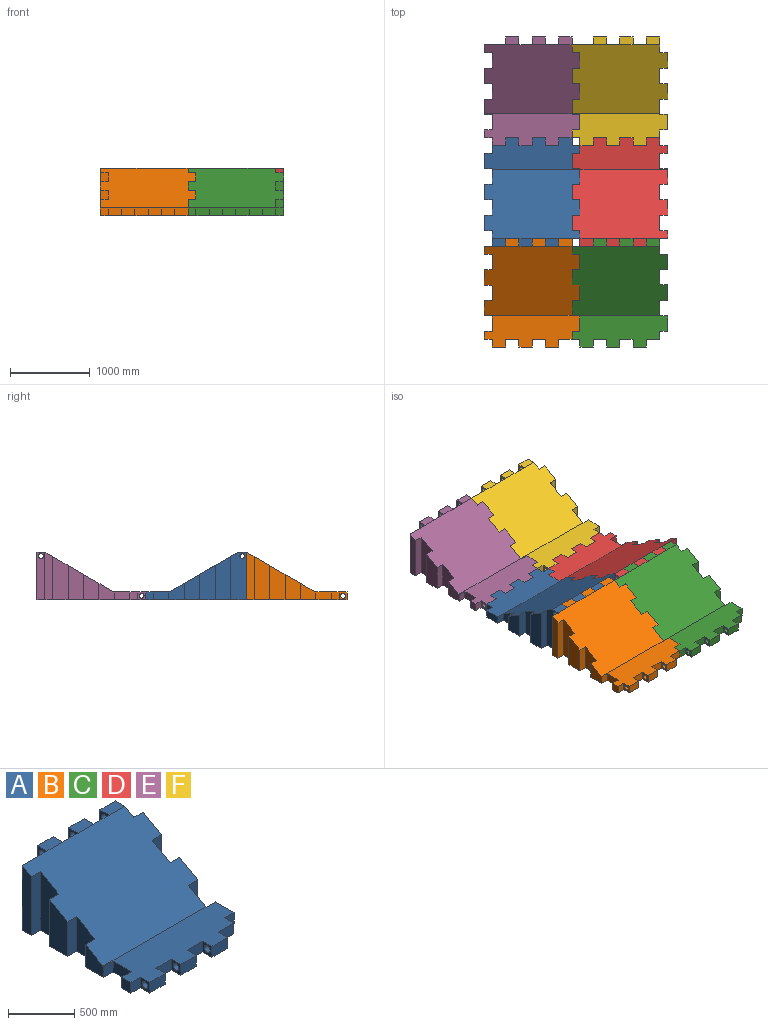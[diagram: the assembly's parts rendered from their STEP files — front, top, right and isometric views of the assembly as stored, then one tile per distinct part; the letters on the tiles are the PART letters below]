
ASSEMBLY  parts=6 mates=8
PART A: 62 faces, bbox 1200x1366x600 mm
  f0: cylinder r=30mm len=166.67mm, axis (-1,0,0), area 31415.9mm2, adj f1,f6
  f1: plane 100x100mm, normal (-1,0,0), area 7172.6mm2, adj f0,f3,f11,f14,f19
  f2: plane 100x100mm, normal (1,0,0), area 7172.6mm2, adj f3,f13,f14,f19,f54
  f3: plane 166.67x100mm, normal (0,-1,0), area 16666.7mm2, adj f1,f2,f14,f19
  f4: plane 100x100mm, normal (0,-1,0), area 10000mm2, adj f5,f14,f19,f20
  f5: plane 100x97.17mm, normal (1,0,0), area 9716.9mm2, adj f4,f7,f14,f19
  f6: plane 100x100mm, normal (1,0,0), area 7172.6mm2, adj f0,f7,f11,f14,f19
  f7: plane 166.67x100mm, normal (0,-1,0), area 16666.7mm2, adj f5,f6,f14,f19
  f8: plane 600x166.67mm, normal (0,1,0), area 100000mm2, adj f14,f15,f49,f52
  f9: plane 600x166.67mm, normal (0,1,0), area 100000mm2, adj f14,f16,f45,f48
  f10: plane 600x166.67mm, normal (0,1,0), area 100000mm2, adj f14,f17,f42,f44
  f11: plane 166.67x100mm, normal (0,-1,0), area 16666.7mm2, adj f1,f6,f14,f19
  f12: plane 166.67x100mm, normal (0,-1,0), area 16666.7mm2, adj f14,f19,f56,f59
  f13: plane 166.67x100mm, normal (0,-1,0), area 16666.7mm2, adj f2,f14,f19,f55
  f14: plane 1366.03x1200mm, normal (0,0,-1), area 1382627.9mm2, adj f1,f2,f3,f4,f5,f6,f7,f8
  f15: plane 166.67x100mm, normal (0,0,1), area 16666.7mm2, adj f8,f18,f49,f52
  f16: plane 166.67x100mm, normal (0,0,1), area 16666.7mm2, adj f9,f18,f45,f48
  f17: plane 166.67x100mm, normal (0,0,1), area 16666.7mm2, adj f10,f18,f42,f44
  f18: plane 1200x866.03mm, normal (0,-0.5,0.87), area 1100000mm2, adj f15,f16,f17,f19,f21,f22,f23,f24
  f19: plane 1200x400mm, normal (0,0,1), area 380000mm2, adj f1,f2,f3,f4,f5,f6,f7,f11
  f20: plane 194.34x100mm, normal (1,0,0), area 19433.8mm2, adj f4,f14,f19,f31
  f21: plane 319.5x194.34mm, normal (1,0,0), area 51188mm2, adj f14,f18,f32,f39
  f22: plane 543.9x194.34mm, normal (1,0,0), area 94797.7mm2, adj f14,f18,f41,f53
  f23: plane 600x97.17mm, normal (-1,0,0), area 55575.7mm2, adj f14,f18,f38,f43
  f24: plane 431.7x194.34mm, normal (-1,0,0), area 72992.9mm2, adj f14,f18,f35,f36
  f25: plane 207.3x194.34mm, normal (-1,0,0), area 29404mm2, adj f14,f18,f19,f29,f33
  f26: plane 100x97.17mm, normal (-1,0,0), area 9716.9mm2, adj f14,f19,f27,f60
  f27: plane 100x100mm, normal (0,1,0), area 10000mm2, adj f14,f19,f26,f28
  f28: plane 194.34x100mm, normal (-1,0,0), area 19433.8mm2, adj f14,f19,f27,f29
  f29: plane 100x100mm, normal (0,-1,0), area 10000mm2, adj f14,f19,f25,f28
  f30: plane 207.3x194.34mm, normal (1,0,0), area 29404mm2, adj f14,f18,f19,f31,f32
  f31: plane 100x100mm, normal (0,1,0), area 10000mm2, adj f14,f19,f20,f30
  f32: plane 207.3x100mm, normal (0,-1,0), area 20729.7mm2, adj f14,f18,f21,f30
  f33: plane 207.3x100mm, normal (0,1,0), area 20729.7mm2, adj f14,f18,f25,f34
  f34: plane 319.5x194.34mm, normal (-1,0,0), area 51188mm2, adj f14,f18,f33,f35
  f35: plane 319.5x100mm, normal (0,-1,0), area 31949.8mm2, adj f14,f18,f24,f34
  f36: plane 431.7x100mm, normal (0,1,0), area 43169.9mm2, adj f14,f18,f24,f37
  f37: plane 543.9x194.34mm, normal (-1,0,0), area 94797.7mm2, adj f14,f18,f36,f38
  f38: plane 543.9x100mm, normal (0,-1,0), area 54390mm2, adj f14,f18,f23,f37
  f39: plane 319.5x100mm, normal (0,1,0), area 31949.8mm2, adj f14,f18,f21,f40
  f40: plane 431.7x194.34mm, normal (1,0,0), area 72992.9mm2, adj f14,f18,f39,f41
  f41: plane 431.7x100mm, normal (0,-1,0), area 43169.9mm2, adj f14,f18,f22,f40
  f42: plane 600x100mm, normal (-1,0,0), area 57172.6mm2, adj f10,f14,f17,f43,f61
  f43: plane 600x266.67mm, normal (0,1,0), area 160000mm2, adj f14,f18,f23,f42
  f44: plane 600x100mm, normal (1,0,0), area 57172.6mm2, adj f10,f14,f17,f46,f61
  f45: plane 600x100mm, normal (-1,0,0), area 57172.6mm2, adj f9,f14,f16,f46,f47
  f46: plane 600x166.67mm, normal (0,1,0), area 100000mm2, adj f14,f18,f44,f45
  f47: cylinder r=30mm len=166.67mm, axis (-1,0,0), area 31415.9mm2, adj f45,f48
  f48: plane 600x100mm, normal (1,0,0), area 57172.6mm2, adj f9,f14,f16,f47,f50
  f49: plane 600x100mm, normal (-1,0,0), area 57172.6mm2, adj f8,f14,f15,f50,f51
  f50: plane 600x166.67mm, normal (0,1,0), area 100000mm2, adj f14,f18,f48,f49
  f51: cylinder r=30mm len=166.67mm, axis (-1,0,0), area 31415.9mm2, adj f49,f52
  f52: plane 600x197.17mm, normal (1,0,0), area 112748.2mm2, adj f8,f14,f15,f18,f51,f53
  f53: plane 543.9x100mm, normal (0,1,0), area 54390mm2, adj f14,f18,f22,f52
  f54: cylinder r=30mm len=166.67mm, axis (-1,0,0), area 31415.9mm2, adj f2,f55
  f55: plane 100x100mm, normal (-1,0,0), area 7172.6mm2, adj f13,f14,f19,f54,f57
  f56: plane 100x100mm, normal (1,0,0), area 7172.6mm2, adj f12,f14,f19,f57,f58
  f57: plane 166.67x100mm, normal (0,-1,0), area 16666.7mm2, adj f14,f19,f55,f56
  f58: cylinder r=30mm len=166.67mm, axis (-1,0,0), area 31415.9mm2, adj f56,f59
  f59: plane 100x100mm, normal (-1,0,0), area 7172.6mm2, adj f12,f14,f19,f58,f60
  f60: plane 100x100mm, normal (0,-1,0), area 10000mm2, adj f14,f19,f26,f59
  f61: cylinder r=30mm len=166.67mm, axis (-1,0,0), area 31415.9mm2, adj f42,f44
PART B: same geometry as A
PART C: same geometry as A
PART D: same geometry as A
PART E: same geometry as A
PART F: same geometry as A
PLACE A rot(axis=(0,0,1),180deg) t=(677.85,1809.4,109.45)mm
PLACE B t=(-522.15,-369.06,109.45)mm fixed
PLACE C t=(577.85,-369.06,109.45)mm
PLACE D rot(axis=(0,0,1),180deg) t=(1777.85,1809.4,109.45)mm
PLACE E t=(-522.15,2162.99,109.45)mm
PLACE F t=(577.85,2162.99,109.45)mm
MATE planar F.f37 <-> E.f22  axis (-1,0,0) through (677.85,3011.61,354.43)mm
MATE planar B.f14 <-> E.f14  axis (0,0,-1) through (77.85,87.16,109.45)mm
MATE planar C.f28 <-> B.f20  axis (-1,0,0) through (677.85,-301.52,159.45)mm
MATE planar B.f40 <-> C.f24  axis (1,0,0) through (577.85,286.33,298.65)mm
MATE planar A.f9 <-> B.f46  axis (0,-1,0) through (-5.49,670.17,409.45)mm
MATE planar D.f57 <-> F.f11  axis (0,1,0) through (1427.85,1936.2,159.45)mm
MATE planar D.f46 <-> C.f9  axis (0,-1,0) through (1261.18,770.17,409.45)mm
MATE planar A.f57 <-> E.f11  axis (0,1,0) through (327.85,1936.2,159.45)mm
